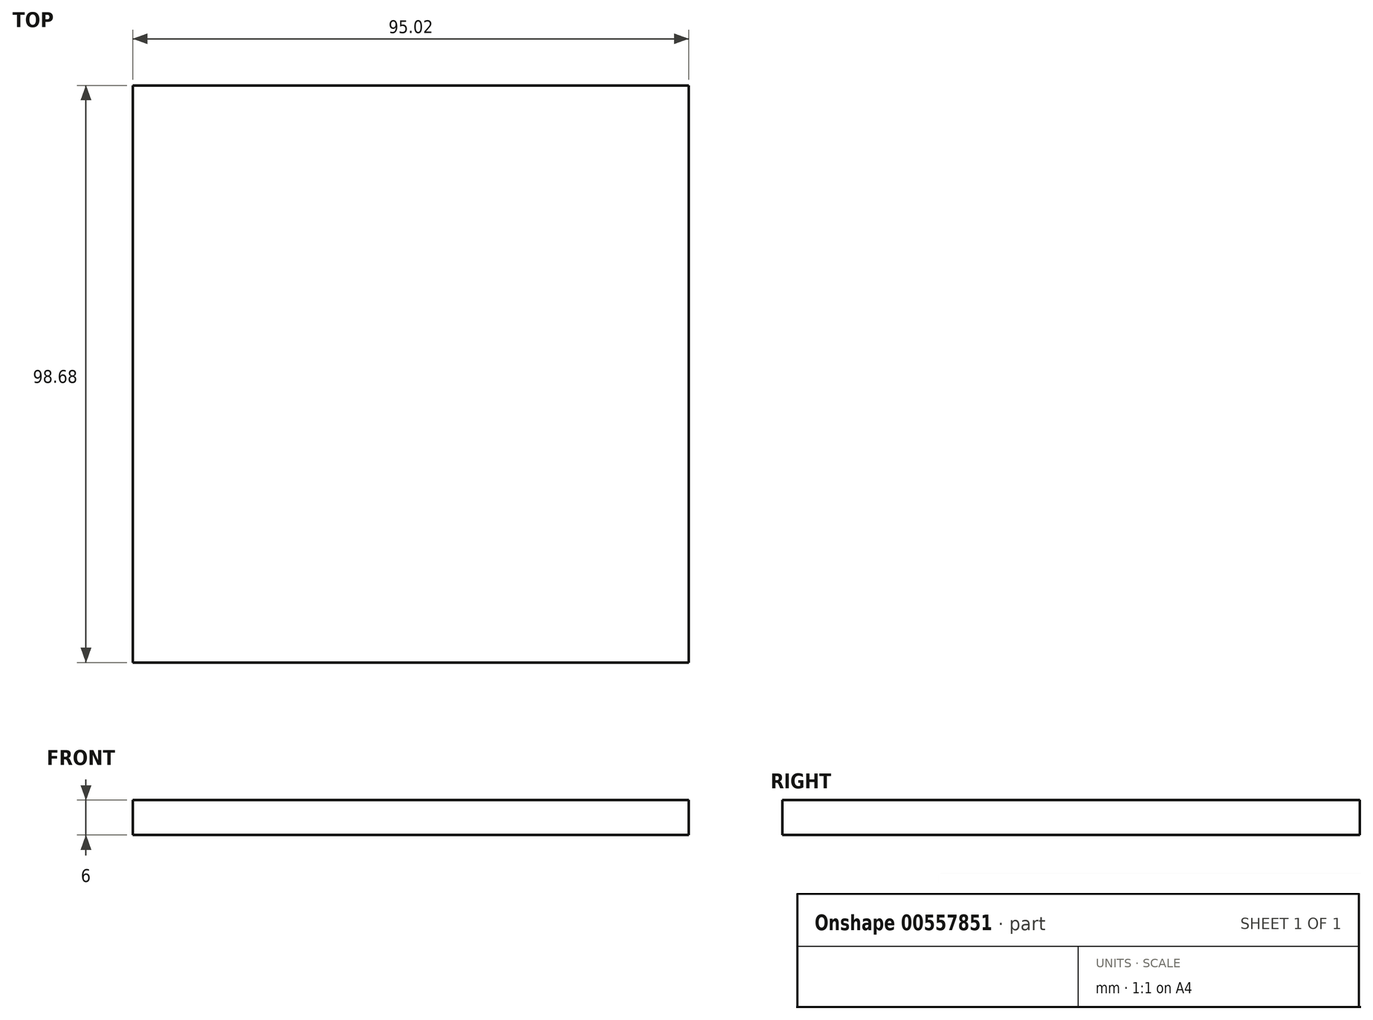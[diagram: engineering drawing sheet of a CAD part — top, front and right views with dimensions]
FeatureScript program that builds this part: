
annotation { "Feature Type Name" : "Feature", "Feature Type Description" : "" }
export const myFeature = defineFeature(function(context is Context, id is Id, definition is map)
    precondition{}
    {
        {
            var Q0;
            Q0=qCreatedBy(makeId("Top.planeOp"),FACE);
            var sketch = newSketch(context, id + "F0", { "sketchPlane" : qUnion([Q0])});
            skLineSegment(sketch, "E0.bottom", {"start": v(47.51, -49.34) * mm, "end": v(-47.51, -49.34) * mm});
            skLineSegment(sketch, "E0.top", {"start": v(47.51, 49.34) * mm, "end": v(-47.51, 49.34) * mm});
            skLineSegment(sketch, "E0.left", {"start": v(47.51, -49.34) * mm, "end": v(47.51, 49.34) * mm});
            skLineSegment(sketch, "E0.right", {"start": v(-47.51, -49.34) * mm, "end": v(-47.51, 49.34) * mm});
            skPoint(sketch, "E0.middle", {"position": v(0, 0) * mm});
            skSolve(sketch);
        }
        {
            var Q0;
            Q0=makeQuery(id+"F0.imprint","IMPRINT",FACE,{"disambiguationData":[TD([[makeQuery(id+"F0.imprint","IMPRINT",EDGE,{"derivedFrom":sQuery(id+"F0.wireOp",EDGE,"E0.bottom")}),-1.0]])]});
            extrude(context, id + "F1", {"entities" : qUnion([Q0]), "depth" : 6 * mm, "offsetDistance" : 25 * mm});
        }
    });
